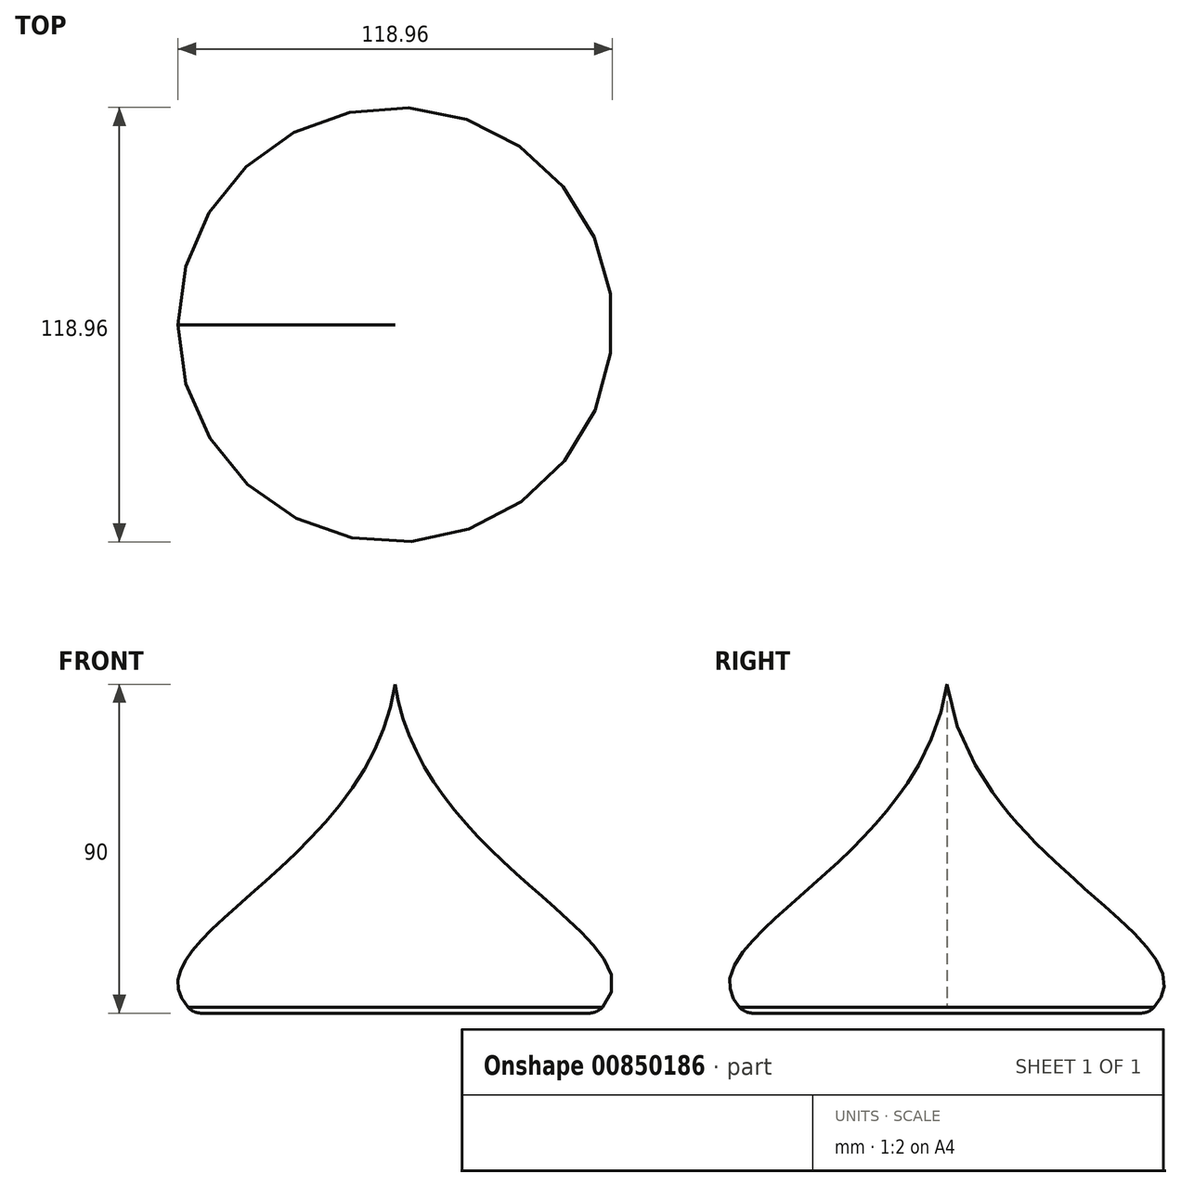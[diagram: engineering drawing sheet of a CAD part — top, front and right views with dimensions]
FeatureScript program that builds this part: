
annotation { "Feature Type Name" : "Feature", "Feature Type Description" : "" }
export const myFeature = defineFeature(function(context is Context, id is Id, definition is map)
    precondition{}
    {
        {
            var Q0;
            Q0=qCreatedBy(makeId("Front.planeOp"),FACE);
            var sketch = newSketch(context, id + "F0", { "sketchPlane" : qUnion([Q0])});
            skLineSegment(sketch, "E0", {"start": v(0, 90) * mm, "end": v(0, 90) * mm});
            skLineSegment(sketch, "E1", {"start": v(0, 0) * mm, "end": v(-55, 0) * mm});
            skFitSpline(sketch, "E2", {"points": [v(0, 90) * mm, v(-55, 0) * mm], "startDerivative": vector(-22.66, -152.3) * mm, "endDerivative": vector(67.85, -57.54) * mm});
            skLineSegment(sketch, "E3", {"start": v(0, 90) * mm, "end": v(0, 0) * mm});
            skSolve(sketch);
        }
        {
            var Q0;
            Q0 = qSketchRegion(id + "F0", true);
            var Q1;
            Q1=sQuery(id+"F0.wireOp",EDGE,"E3");
            revolve(context, id + "F1", {"surfaceOperationType" : NewSurfaceOperationType.NEW, "entities" : qUnion([Q0]), "axis" : qUnion([Q1]), "revolveType" : RevolveType.FULL});
        }
        {
            var Q0;
            Q0=makeQuery(id+"F1.opRevolve","SWEPT_EDGE",EDGE,{"disambiguationData":[OSD([sQuery(id+"F0.wireOp",EDGE,"E0"),sQuery(id+"F0.wireOp",EDGE,"E2")])]});
            fillet(context, id + "F2", {"entities" : qUnion([Q0]), "radius" : 5 * mm, "tangentPropagation" : true, "allowEdgeOverflow" : false});
        }
    });
